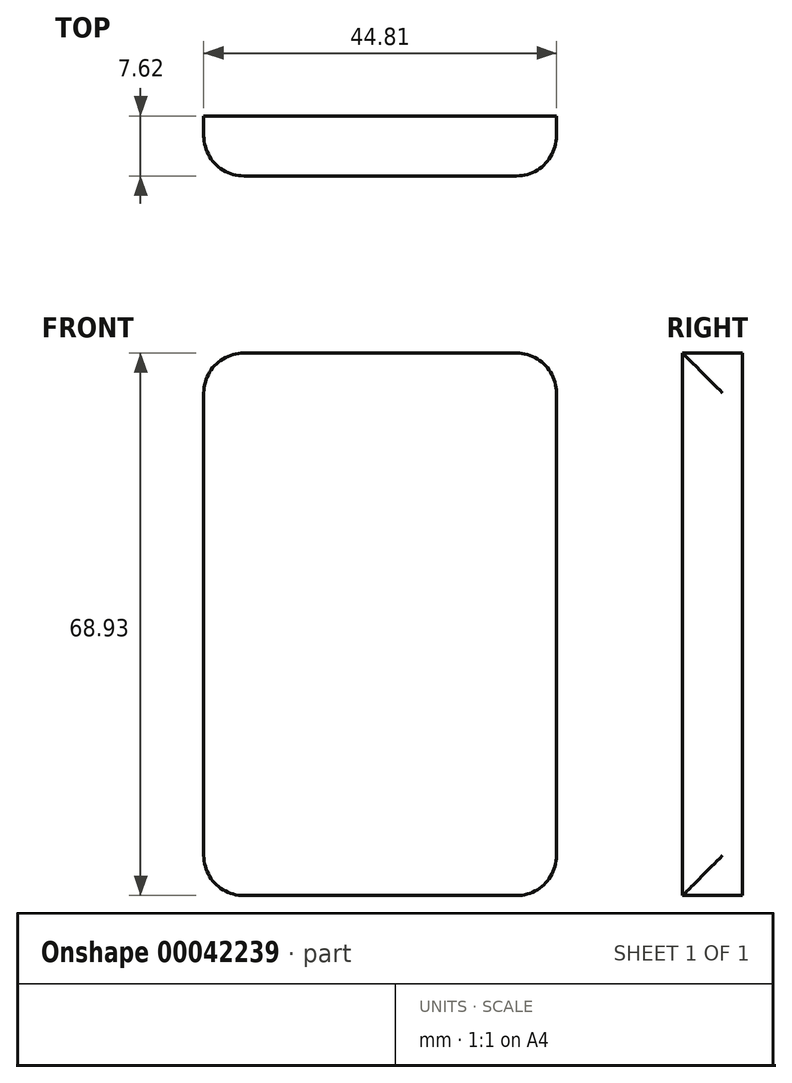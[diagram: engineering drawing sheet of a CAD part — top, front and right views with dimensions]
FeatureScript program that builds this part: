
annotation { "Feature Type Name" : "Feature", "Feature Type Description" : "" }
export const myFeature = defineFeature(function(context is Context, id is Id, definition is map)
    precondition{}
    {
        {
            var Q0;
            Q0=qCreatedBy(makeId("Front.planeOp"),FACE);
            var sketch = newSketch(context, id + "F0", { "sketchPlane" : qUnion([Q0])});
            skLineSegment(sketch, "E0", {"start": v(0, -21.91) * mm, "end": v(-44.8, -21.91) * mm});
            skLineSegment(sketch, "E1", {"start": v(-44.8, -21.91) * mm, "end": v(-44.8, 47.02) * mm});
            skLineSegment(sketch, "E2", {"start": v(-44.8, 47.02) * mm, "end": v(0, 47.02) * mm});
            skLineSegment(sketch, "E3", {"start": v(0, 47.02) * mm, "end": v(0, -21.91) * mm});
            skSolve(sketch);
        }
        {
            var Q0;
            Q0=makeQuery(id+"F0.imprint","IMPRINT",FACE,{"disambiguationData":[TD([[makeQuery(id+"F0.imprint","IMPRINT",EDGE,{"derivedFrom":sQuery(id+"F0.wireOp",EDGE,"E0")}),-1.0]])]});
            extrude(context, id + "F1", {"entities" : qUnion([Q0]), "depth" : 7.62 * mm});
        }
        {
            var Q0;
            Q0=makeQuery(id+"F1.opExtrude","CAP_EDGE",EDGE,{"disambiguationData":[OSD([sQuery(id+"F0.wireOp",EDGE,"E3")])],"isStart":false});
            var Q1;
            Q1=makeQuery(id+"F1.opExtrude","CAP_EDGE",EDGE,{"disambiguationData":[OSD([sQuery(id+"F0.wireOp",EDGE,"E1")])],"isStart":false});
            var Q2;
            Q2=makeQuery(id+"F1.opExtrude","SWEPT_EDGE",EDGE,{"disambiguationData":[OSD([sQuery(id+"F0.wireOp",EDGE,"E2"),sQuery(id+"F0.wireOp",EDGE,"E3")])]});
            var Q3;
            Q3=makeQuery(id+"F1.opExtrude","SWEPT_EDGE",EDGE,{"disambiguationData":[OSD([sQuery(id+"F0.wireOp",EDGE,"E1"),sQuery(id+"F0.wireOp",EDGE,"E2")])]});
            var Q4;
            Q4=makeQuery(id+"F1.opExtrude","SWEPT_EDGE",EDGE,{"disambiguationData":[OSD([sQuery(id+"F0.wireOp",EDGE,"E0"),sQuery(id+"F0.wireOp",EDGE,"E1")])]});
            var Q5;
            Q5=makeQuery(id+"F1.opExtrude","SWEPT_EDGE",EDGE,{"disambiguationData":[OSD([sQuery(id+"F0.wireOp",EDGE,"E0"),sQuery(id+"F0.wireOp",EDGE,"E3")])]});
            fillet(context, id + "F2", {"entities" : qUnion([Q0, Q1, Q2, Q3, Q4, Q5]), "radius" : 5.08 * mm, "tangentPropagation" : true, "allowEdgeOverflow" : false});
        }
    });
